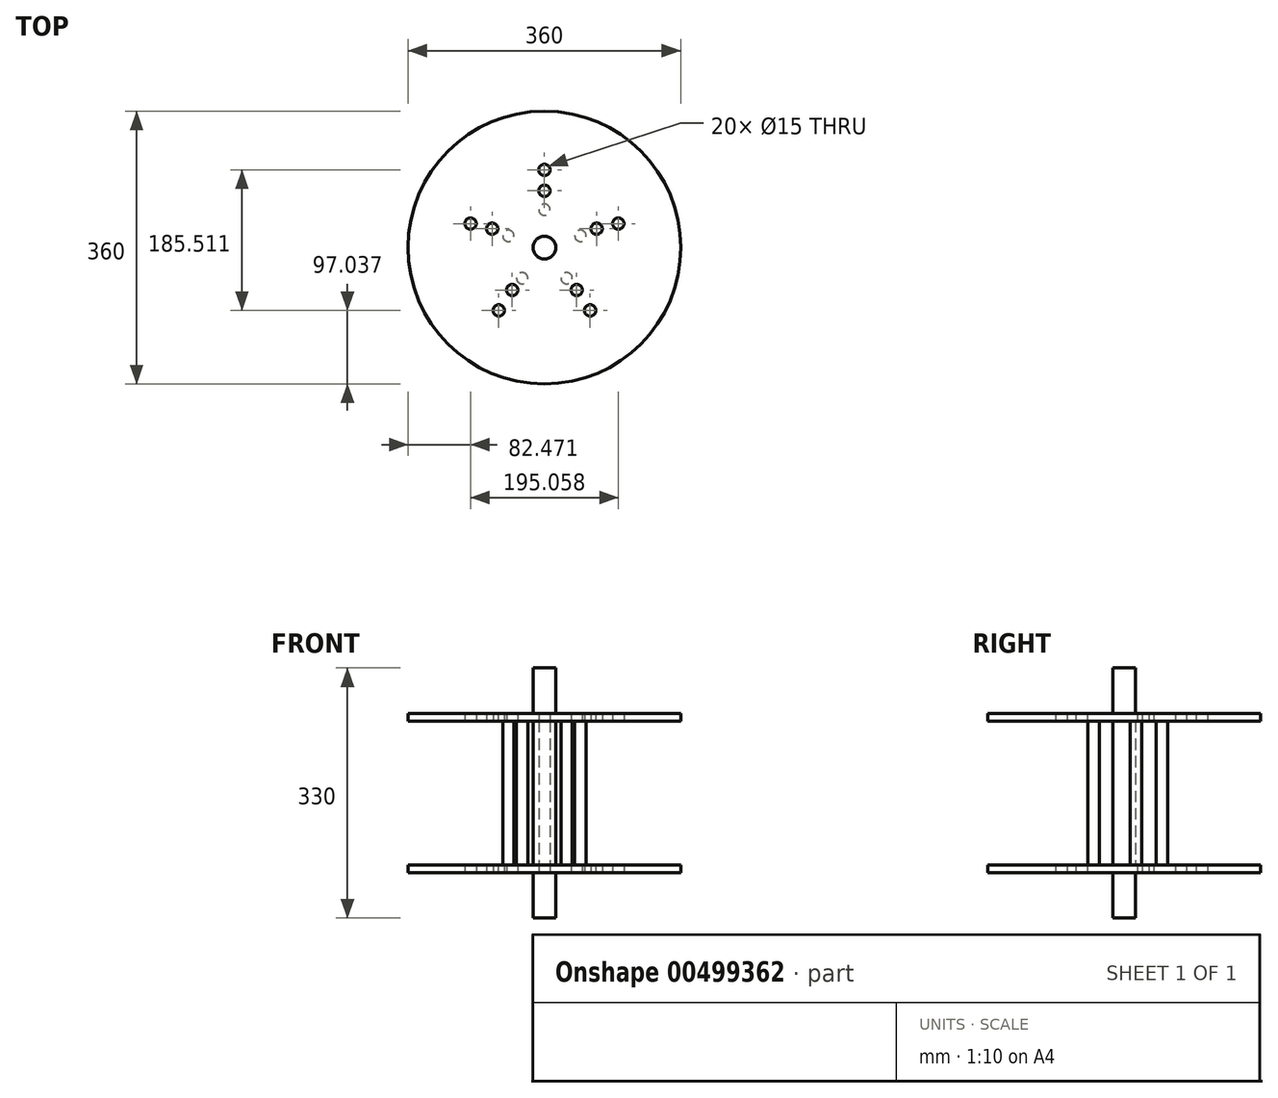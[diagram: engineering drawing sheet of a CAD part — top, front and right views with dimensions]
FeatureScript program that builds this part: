
annotation { "Feature Type Name" : "Feature", "Feature Type Description" : "" }
export const myFeature = defineFeature(function(context is Context, id is Id, definition is map)
    precondition{}
    {
        {
            var Q0;
            Q0=qCreatedBy(makeId("Top.planeOp"),FACE);
            var sketch = newSketch(context, id + "F0", { "sketchPlane" : qUnion([Q0])});
            skCircle(sketch, "E0", {"center": v(0, 0) * mm, "radius": 180 * mm});
            skSolve(sketch);
        }
        {
            var Q0;
            Q0 = qSketchRegion(id + "F0", true);
            extrude(context, id + "F1", {"entities" : qUnion([Q0]), "depth" : 10 * mm});
        }
        {
            var Q0;
            Q0=qCreatedBy(makeId("Top.planeOp"),FACE);
            var sketch = newSketch(context, id + "F2", { "sketchPlane" : qUnion([Q0])});
            skCircle(sketch, "E1", {"center": v(0, 0) * mm, "radius": 15 * mm});
            skCircle(sketch, "E2", {"center": v(0, 50) * mm, "radius": 7.5 * mm});
            skCircle(sketch, "E3.1.0", {"center": v(-47.55, 15.45) * mm, "radius": 7.5 * mm});
            skCircle(sketch, "E3.2.0", {"center": v(-29.39, -40.45) * mm, "radius": 7.5 * mm});
            skCircle(sketch, "E3.3.0", {"center": v(29.39, -40.45) * mm, "radius": 7.5 * mm});
            skCircle(sketch, "E3.4.0", {"center": v(47.55, 15.45) * mm, "radius": 7.5 * mm});
            skSolve(sketch);
        }
        {
            var Q0;
            Q0 = qSketchRegion(id + "F2", true);
            extrude(context, id + "F3", {"entities" : qUnion([Q0]), "operationType" : NewBodyOperationType.ADD, "depth" : 200 * mm});
        }
        {
            var Q0;
            Q0=makeQuery(id+"F3.opExtrude","CAP_FACE",FACE,{"disambiguationData":[OSD([sQuery(id+"F2.wireOp",EDGE,"E1")])],"isStart":false});
            cPlane(context, id + "F4", {"entities" : qUnion([Q0]), "cplaneType" : CPlaneType.OFFSET, "offset" : 0 * mm, "width" : 150 * mm, "height" : 150 * mm});
        }
        {
            var Q0;
            Q0=qCreatedBy(id+"F4.planeOp",FACE);
            var sketch = newSketch(context, id + "F5", { "sketchPlane" : qUnion([Q0])});
            skCircle(sketch, "E4", {"center": v(0, 0) * mm, "radius": 180 * mm});
            skSolve(sketch);
        }
        {
            var Q0;
            Q0 = qSketchRegion(id + "F5", true);
            extrude(context, id + "F6", {"entities" : qUnion([Q0]), "operationType" : NewBodyOperationType.ADD, "depth" : 10 * mm});
        }
        {
            var Q0;
            Q0=qCreatedBy(makeId("Top.planeOp"),FACE);
            var sketch = newSketch(context, id + "F7", { "sketchPlane" : qUnion([Q0])});
            skCircle(sketch, "E5", {"center": v(0, 0) * mm, "radius": 15 * mm});
            skSolve(sketch);
        }
        {
            var Q0;
            Q0 = qSketchRegion(id + "F7", true);
            extrude(context, id + "F8", {"entities" : qUnion([Q0]), "operationType" : NewBodyOperationType.ADD, "oppositeDirection" : true, "depth" : 60 * mm});
        }
        {
            var Q0;
            Q0=makeQuery(id+"F6.opExtrude","CAP_FACE",FACE,{"disambiguationData":[OSD([sQuery(id+"F5.wireOp",EDGE,"E4")])],"isStart":false});
            cPlane(context, id + "F9", {"entities" : qUnion([Q0]), "cplaneType" : CPlaneType.OFFSET, "offset" : 0 * mm, "width" : 150 * mm, "height" : 150 * mm});
        }
        {
            var Q0;
            Q0=qCreatedBy(id+"F9.planeOp",FACE);
            var sketch = newSketch(context, id + "F10", { "sketchPlane" : qUnion([Q0])});
            skCircle(sketch, "E6", {"center": v(0, 0) * mm, "radius": 15 * mm});
            skSolve(sketch);
        }
        {
            var Q0;
            Q0 = qSketchRegion(id + "F10", true);
            extrude(context, id + "F11", {"entities" : qUnion([Q0]), "operationType" : NewBodyOperationType.ADD, "depth" : 60 * mm});
        }
        {
            var Q0;
            Q0=qCreatedBy(makeId("Top.planeOp"),FACE);
            var sketch = newSketch(context, id + "F12", { "sketchPlane" : qUnion([Q0])});
            skCircle(sketch, "E7", {"center": v(0, 75) * mm, "radius": 7.5 * mm});
            skCircle(sketch, "E8.1.0", {"center": v(-68.9, 24.94) * mm, "radius": 7.5 * mm});
            skCircle(sketch, "E8.2.0", {"center": v(-42.59, -56.07) * mm, "radius": 7.5 * mm});
            skCircle(sketch, "E8.3.0", {"center": v(42.59, -56.07) * mm, "radius": 7.5 * mm});
            skCircle(sketch, "E8.4.0", {"center": v(68.9, 24.94) * mm, "radius": 7.5 * mm});
            skPoint(sketch, "E8.center", {"position": v(0, 2.55) * mm});
            skCircle(sketch, "E9", {"center": v(0, 102.55) * mm, "radius": 7.5 * mm});
            skCircle(sketch, "E10.1.0", {"center": v(-97.53, 31.69) * mm, "radius": 7.5 * mm});
            skCircle(sketch, "E10.2.0", {"center": v(-60.28, -82.96) * mm, "radius": 7.5 * mm});
            skCircle(sketch, "E10.3.0", {"center": v(60.28, -82.96) * mm, "radius": 7.5 * mm});
            skCircle(sketch, "E10.4.0", {"center": v(97.53, 31.69) * mm, "radius": 7.5 * mm});
            skPoint(sketch, "E10.center", {"position": v(0, 0) * mm});
            skSolve(sketch);
        }
        {
            var Q0;
            Q0 = qSketchRegion(id + "F12", true);
            extrude(context, id + "F13", {"entities" : qUnion([Q0]), "operationType" : NewBodyOperationType.REMOVE, "depth" : 220 * mm});
        }
    });
